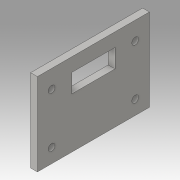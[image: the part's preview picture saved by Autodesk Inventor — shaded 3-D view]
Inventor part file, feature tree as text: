
AUTODESK INVENTOR PART (.ipt)
format: ipt  version: 2016 (Build 200138000, 138)  size: 105,984 bytes
history: native  units: in
note: dims shown in document units (in); Inventor stores cm internally (conversion verified against a paired STEP export)
features: sketch x3, extrude x2, hole x1
ambient origin geometry x8: Origin, YZ Plane, XZ Plane, XY Plane, X Axis, Y Axis, Z Axis, Center Point
bodies: Solid1 (feature_tree)
feature tree (6):
  extrude  "Extrusion1"  Depth=2.287in
  hole  "Hole1"  [1 undecoded]
  extrude  "Extrusion2"  Depth=0.3937in
  sketch  "Sketch1"  dims[d0=3.102in d1=2.287in]
  sketch  "Sketch2"  dims[d2=0.188in d3=0.0in d4=0.3937in]
  sketch  "Sketch3"  dims[d6=0.3937in d7=0.3937in d9=0.3937in d10=0.5in d12=0.5in d16=0.3937in d17=0.3937in d18=0.188in d19=0.75in d20=0.375in d21=0.25in d22=0.5635in d23=1.0in d24=0.8108in d25=0.515in d26=1.2in d28=3.102in d29=0.951in d30=2.287in d31=0.375in d32=0.198in d33=0.0in]
note: 1 required parameter value undecoded (feature->parameter linkage not recoverable at this tier; creation-order binding heuristic only, values carry confidence <= 0.55)
